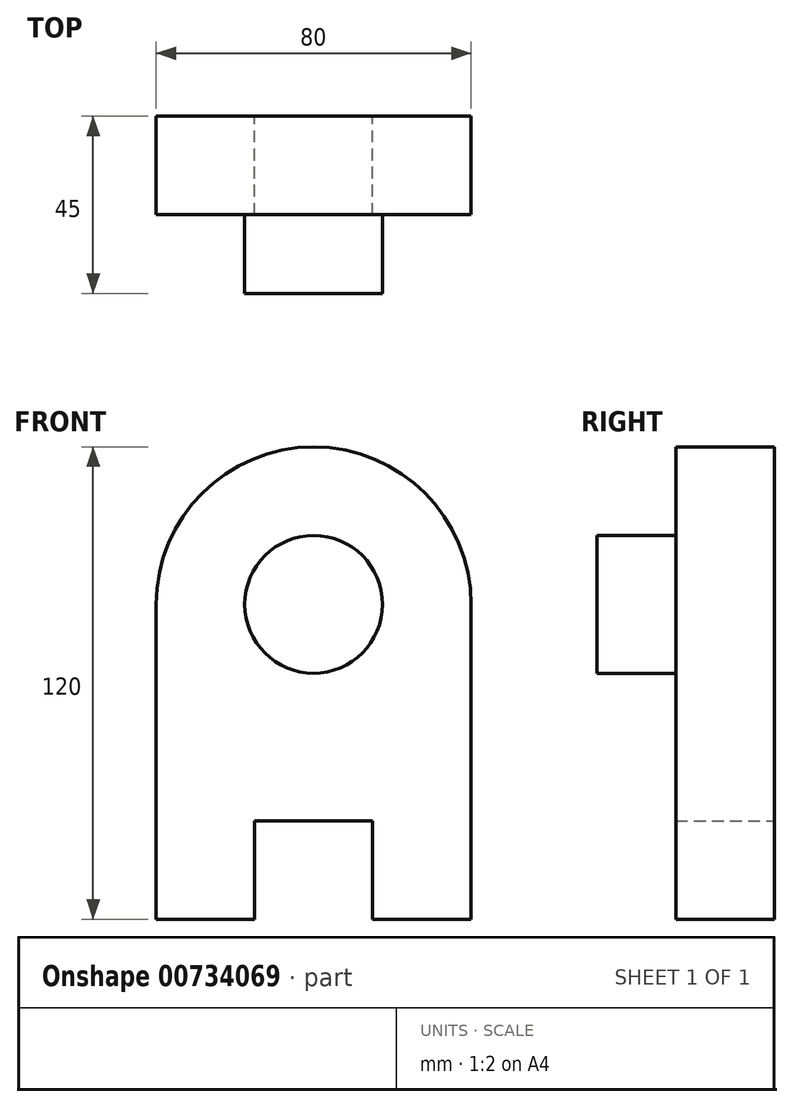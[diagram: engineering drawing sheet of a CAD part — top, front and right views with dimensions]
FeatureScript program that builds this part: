
annotation { "Feature Type Name" : "Feature", "Feature Type Description" : "" }
export const myFeature = defineFeature(function(context is Context, id is Id, definition is map)
    precondition{}
    {
        {
            var Q0;
            Q0=qCreatedBy(makeId("Front.planeOp"),FACE);
            var sketch = newSketch(context, id + "F0", { "sketchPlane" : qUnion([Q0])});
            skLineSegment(sketch, "E0.bottom", {"start": v(40, -40) * mm, "end": v(15, -40) * mm});
            skLineSegment(sketch, "E0.left", {"start": v(40, -40) * mm, "end": v(40, 40) * mm});
            skLineSegment(sketch, "E0.right", {"start": v(-40, -40) * mm, "end": v(-40, 40) * mm});
            skPoint(sketch, "E0.middle", {"position": v(0, 0) * mm});
            skLineSegment(sketch, "E1", {"start": v(-40, -40) * mm, "end": v(-15, -40) * mm});
            skLineSegment(sketch, "E2", {"start": v(-15, -40) * mm, "end": v(-15, -15) * mm});
            skLineSegment(sketch, "E3", {"start": v(-15, -15) * mm, "end": v(15, -15) * mm});
            skLineSegment(sketch, "E4", {"start": v(15, -15) * mm, "end": v(15, -40) * mm});
            skLineSegment(sketch, "E5.trimOffspring", {"start": v(-15, -40) * mm, "end": v(-40, -40) * mm});
            skArc(sketch, "E6", {"start": v(0, 80) * mm, "mid": v(-28.28, 68.28) * mm, "end": v(-40, 40) * mm});
            skArc(sketch, "E7", {"start": v(40, 40) * mm, "mid": v(28.28, 68.28) * mm, "end": v(0, 80) * mm});
            skSolve(sketch);
        }
        {
            var Q0;
            Q0=makeQuery(id+"F0.imprint","IMPRINT",FACE,{"disambiguationData":[TD([[makeQuery(id+"F0.imprint","IMPRINT",EDGE,{"derivedFrom":sQuery(id+"F0.wireOp",EDGE,"E0.bottom")}),-1.0]])]});
            extrude(context, id + "F1", {"entities" : qUnion([Q0]), "depth" : 25 * mm, "offsetDistance" : 25 * mm});
        }
        {
            var Q0;
            Q0=makeQuery(id+"F1.opExtrude","CAP_FACE",FACE,{"disambiguationData":[OSD([sQuery(id+"F0.wireOp",EDGE,"E0.bottom"),sQuery(id+"F0.wireOp",EDGE,"E0.left"),sQuery(id+"F0.wireOp",EDGE,"E0.right"),sQuery(id+"F0.wireOp",EDGE,"E2"),sQuery(id+"F0.wireOp",EDGE,"E3"),sQuery(id+"F0.wireOp",EDGE,"E4"),sQuery(id+"F0.wireOp",EDGE,"E5.trimOffspring"),sQuery(id+"F0.wireOp",EDGE,"E6"),sQuery(id+"F0.wireOp",EDGE,"E7")])],"isStart":false});
            var sketch = newSketch(context, id + "F2", { "sketchPlane" : qUnion([Q0])});
            skCircle(sketch, "E8", {"center": v(0, 40) * mm, "radius": 17.5 * mm});
            skSolve(sketch);
        }
        {
            var Q0;
            Q0 = qSketchRegion(id + "F2", true);
            extrude(context, id + "F3", {"entities" : qUnion([Q0]), "operationType" : NewBodyOperationType.ADD, "depth" : 20 * mm, "offsetDistance" : 25 * mm});
        }
    });
